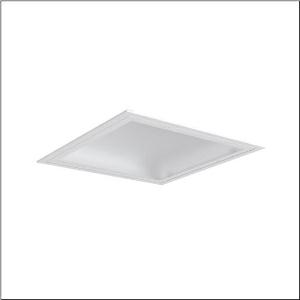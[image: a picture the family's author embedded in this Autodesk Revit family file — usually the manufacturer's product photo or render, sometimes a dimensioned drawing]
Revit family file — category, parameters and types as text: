
# Revit family: mira_r__21_51fr427a432a_cde4
name_source: partatom
category: Lighting Fixtures
units: mm (PartAtom-declared; Revit-internal decimal feet)

## family parameters
Cut with Voids When Loaded = No
Host = Face
Light Source = No
Part Type = Normal
Room Calculation Point = No
Round Connector Dimension = Use Diameter
Shared = No

## types (1)
- Mira® 21 (1 x LED, 3220 lm, 23 W, 4000K)
    Apparent Load = 23 VA
    CIE Flux Codes = 50 81 97 100 100
    Color Rendering = 80
    Color Temperature = 4000K
    Default Elevation = 1800 mm
    Description = Mira® 21, clean room luminaire, primary light control with reflector, primary optical cover: cover, of PC, light emission: direct distribution, primary light characteristic: symmetric, installation type: recessed, LED, rated luminous flux: 3.220lm, luminous efficacy: 140lm/W, light colour: 840, colour temperature: 4000K, control gear: ECG, with terminal, 3-pole, max. 2.5mm², mains connection: 230V, AC, 50/60Hz, rated input power: 23W, luminaire housing, of sheet steel, coated, pure white (RAL 9010), with concealed spring brackets, module: M625, length: 623mm, width: 623mm, height: 115mm, protection rating (complete): IP54, insulation class (complete): insulation class I (protective earthing), certification: CE, UKCA, permissible operating ambient temperature: -5..+40°C, standard: EN 50419, packaging unit: 1 piece
    Height = 0 mm  [stored 0 ft]
    Lamp = 1 x LED
    Lamp Light Flux = 3220 lm
    Lamp Power = 23 W
    Lamp count = 1
    Length = 625 mm
    Luminous efficacy = 140 lm/W
    Manufacturer = Siteco
    ModVariant = No
    Model = 51FR427A432A
    Mounting Place = Ceiling
    Mounting Type = Recessed
    Number of Poles = 1
    OnlyDefault = Yes
    Power Factor = 1
    Product Name = Mira® 21
    Product group = clean room luminaire
    ProductGroupID = 402
    Protection Class = Protection class I
    Protection Degree = IP 54
    RLX_Detail_Level = 1
    RLX_Emergency_Light_Flux = 0 lm
    RLX_Emergency_Type = 0
    RLX_Emergency_Type_DB = No
    RlxData = <blob elided: 13373 chars, md5=07c19ae3>
    Socket = socket
    Standby Power = 0 W
    System Light Flux = 3220 lm
    System Power = 23 W
    Type Comments = Product without accessories
    Type Image = l_1007109.jpg
    URL = http://relux.com
    VarID = ---
    Voltage = 0 V
    Weight = 0.00 kg
    Width = 625 mm

note: [stored X ft] marks values corroborated as IEEE doubles in the binary element streams (Revit-internal decimal feet)

## geometry (parser evidence)
native form markers: Sweep x10
no freeform markers — native parametric forms only
